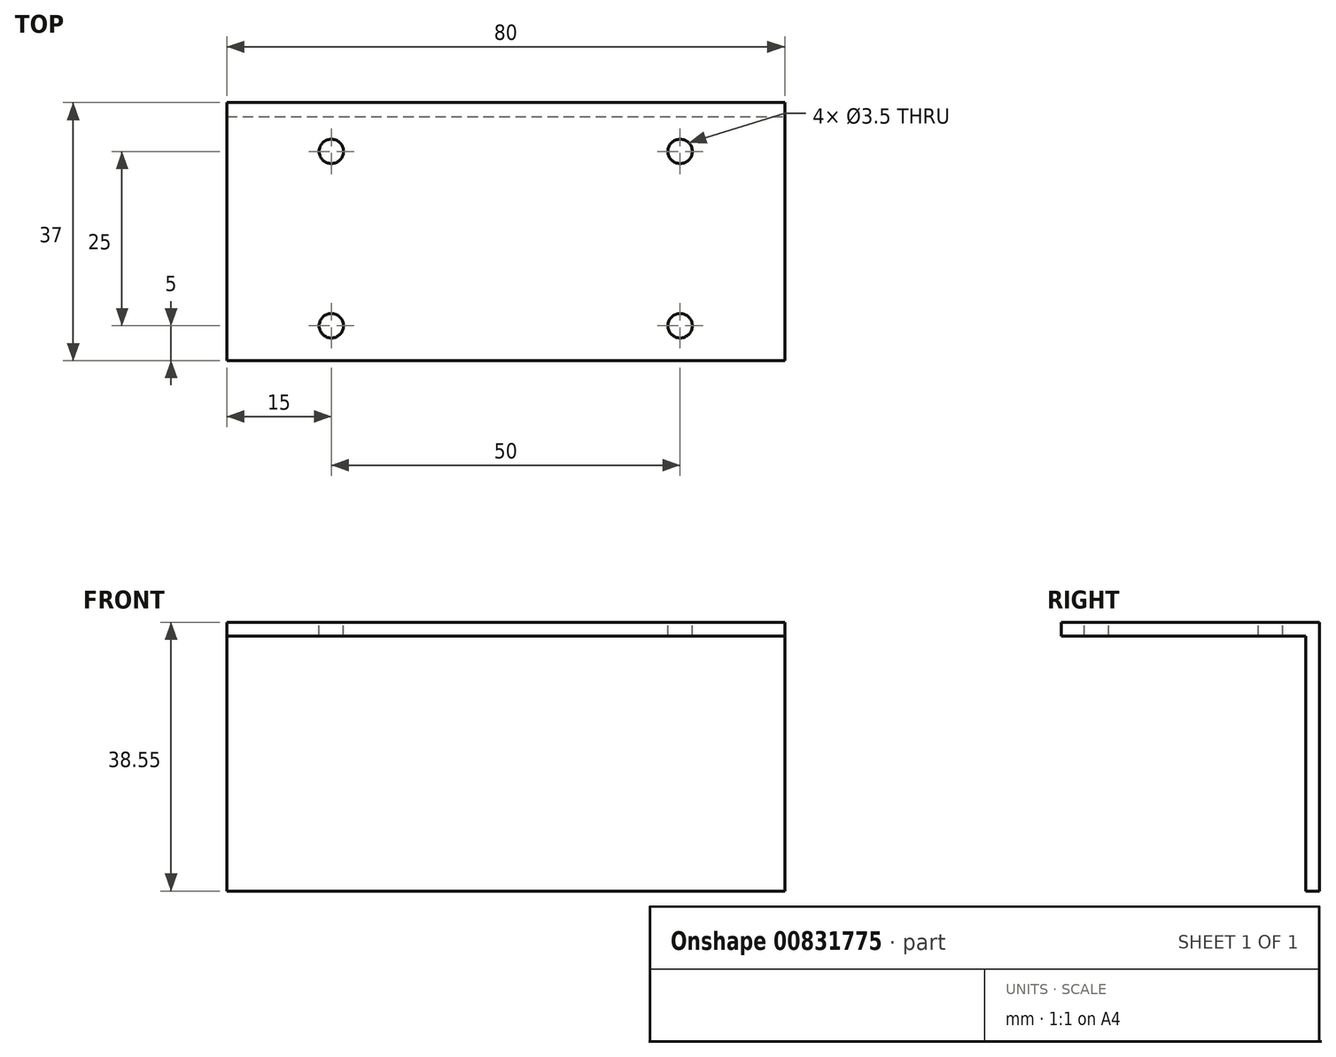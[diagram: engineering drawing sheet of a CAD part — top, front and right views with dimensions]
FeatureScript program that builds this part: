
annotation { "Feature Type Name" : "Feature", "Feature Type Description" : "" }
export const myFeature = defineFeature(function(context is Context, id is Id, definition is map)
    precondition{}
    {
        {
            var Q0;
            Q0=qCreatedBy(makeId("Top.planeOp"),FACE);
            var sketch = newSketch(context, id + "F0", { "sketchPlane" : qUnion([Q0])});
            skLineSegment(sketch, "E0.bottom", {"start": v(0, 0) * mm, "end": v(60, 0) * mm});
            skLineSegment(sketch, "E0.top", {"start": v(0, 35) * mm, "end": v(60, 35) * mm});
            skLineSegment(sketch, "E0.left", {"start": v(0, 0) * mm, "end": v(0, 35) * mm});
            skLineSegment(sketch, "E0.right", {"start": v(60, 0) * mm, "end": v(60, 35) * mm});
            skSolve(sketch);
        }
        {
            var Q0;
            Q0=makeQuery(id+"F0.imprint","IMPRINT",FACE,{"disambiguationData":[TD([[makeQuery(id+"F0.imprint","IMPRINT",EDGE,{"derivedFrom":sQuery(id+"F0.wireOp",EDGE,"E0.bottom")}),1.0]])]});
            extrude(context, id + "F1", {"entities" : qUnion([Q0]), "depth" : 2 * mm, "offsetDistance" : 25 * mm});
        }
        {
            var Q0;
            Q0=makeQuery(id+"F1.opExtrude","CAP_FACE",FACE,{"disambiguationData":[OSD([sQuery(id+"F0.wireOp",EDGE,"E0.bottom"),sQuery(id+"F0.wireOp",EDGE,"E0.top"),sQuery(id+"F0.wireOp",EDGE,"E0.left"),sQuery(id+"F0.wireOp",EDGE,"E0.right")])],"isStart":false});
            var sketch = newSketch(context, id + "F2", { "sketchPlane" : qUnion([Q0])});
            skLineSegment(sketch, "E1.bottom", {"start": v(5, 30) * mm, "end": v(55, 30) * mm, "construction": true});
            skLineSegment(sketch, "E1.top", {"start": v(5, 5) * mm, "end": v(55, 5) * mm, "construction": true});
            skLineSegment(sketch, "E1.left", {"start": v(5, 30) * mm, "end": v(5, 5) * mm, "construction": true});
            skLineSegment(sketch, "E1.right", {"start": v(55, 30) * mm, "end": v(55, 5) * mm, "construction": true});
            skCircle(sketch, "E2", {"center": v(5, 30) * mm, "radius": 1.75 * mm});
            skCircle(sketch, "E3", {"center": v(5, 5) * mm, "radius": 1.75 * mm});
            skCircle(sketch, "E4", {"center": v(55, 5) * mm, "radius": 1.75 * mm});
            skCircle(sketch, "E5", {"center": v(55, 30) * mm, "radius": 1.75 * mm});
            skSolve(sketch);
        }
        {
            var Q0;
            Q0=makeQuery(id+"F2.imprint","IMPRINT",FACE,{"disambiguationData":[TD([[makeQuery(id+"F2.imprint","IMPRINT",EDGE,{"derivedFrom":sQuery(id+"F2.wireOp",EDGE,"E3")}),1.0]])]});
            var Q1;
            Q1=makeQuery(id+"F2.imprint","IMPRINT",FACE,{"disambiguationData":[TD([[makeQuery(id+"F2.imprint","IMPRINT",EDGE,{"derivedFrom":sQuery(id+"F2.wireOp",EDGE,"E2")}),1.0]])]});
            var Q2;
            Q2=makeQuery(id+"F2.imprint","IMPRINT",FACE,{"disambiguationData":[TD([[makeQuery(id+"F2.imprint","IMPRINT",EDGE,{"derivedFrom":sQuery(id+"F2.wireOp",EDGE,"E5")}),1.0]])]});
            var Q3;
            Q3=makeQuery(id+"F2.imprint","IMPRINT",FACE,{"disambiguationData":[TD([[makeQuery(id+"F2.imprint","IMPRINT",EDGE,{"derivedFrom":sQuery(id+"F2.wireOp",EDGE,"E4")}),1.0]])]});
            extrude(context, id + "F3", {"entities" : qUnion([Q0, Q1, Q2, Q3]), "operationType" : NewBodyOperationType.REMOVE, "endBound" : BoundingType.THROUGH_ALL, "oppositeDirection" : true, "depth" : 25 * mm, "offsetDistance" : 25 * mm});
        }
        {
            var Q0;
            Q0=makeQuery(id+"F1.opExtrude","SWEPT_FACE",FACE,{"disambiguationData":[OSD([sQuery(id+"F0.wireOp",EDGE,"E0.right")])]});
            extrude(context, id + "F4", {"entities" : qUnion([Q0]), "operationType" : NewBodyOperationType.ADD, "depth" : 10 * mm, "offsetDistance" : 25 * mm});
        }
        {
            var Q0;
            Q0=makeQuery(id+"F1.opExtrude","SWEPT_FACE",FACE,{"disambiguationData":[OSD([sQuery(id+"F0.wireOp",EDGE,"E0.left")])]});
            extrude(context, id + "F5", {"entities" : qUnion([Q0]), "operationType" : NewBodyOperationType.ADD, "depth" : 10 * mm, "offsetDistance" : 25 * mm});
        }
        {
            var Q0;
            {var subQ0=sQuery(id+"F0.wireOp",EDGE,"E0.top");Q0=makeQuery(id+"F5.boolean.opBoolean","MERGE",FACE,{"derivedFrom":[makeQuery(id+"F4.boolean.opBoolean","MERGE",FACE,{"derivedFrom":[makeQuery(id+"F1.opExtrude","SWEPT_FACE",FACE,{"disambiguationData":[OSD([subQ0])]}),makeQuery(id+"F4.opExtrude","SWEPT_FACE",FACE,{"disambiguationData":[OSD([subQ0,sQuery(id+"F0.wireOp",EDGE,"E0.right")])]})]}),makeQuery(id+"F5.opExtrude","SWEPT_FACE",FACE,{"disambiguationData":[OSD([subQ0,sQuery(id+"F0.wireOp",EDGE,"E0.left")])]})]});}
            var sketch = newSketch(context, id + "F6", { "sketchPlane" : qUnion([Q0])});
            skLineSegment(sketch, "E6.bottom", {"start": v(-70, 2) * mm, "end": v(10, 2) * mm});
            skLineSegment(sketch, "E6.top", {"start": v(-70, -36.55) * mm, "end": v(10, -36.55) * mm});
            skLineSegment(sketch, "E6.left", {"start": v(-70, 2) * mm, "end": v(-70, -36.55) * mm});
            skLineSegment(sketch, "E6.right", {"start": v(10, 2) * mm, "end": v(10, -36.55) * mm});
            skSolve(sketch);
        }
        {
            var Q0;
            {var subQ0=sQuery(id+"F6.wireOp",EDGE,"E6.top");Q0=makeQuery(id+"F6.imprint","IMPRINT",FACE,{"disambiguationData":[TD([[makeQuery(id+"F6.imprint","IMPRINT",EDGE,{"derivedFrom":subQ0}),1.0]])]});}
            var Q1;
            {var subQ0=sQuery(id+"F6.wireOp",EDGE,"E6.bottom");Q1=makeQuery(id+"F6.imprint","IMPRINT",FACE,{"disambiguationData":[TD([[makeQuery(id+"F6.imprint","IMPRINT",EDGE,{"derivedFrom":subQ0}),1.0]])]});}
            extrude(context, id + "F7", {"entities" : qUnion([Q0, Q1]), "operationType" : NewBodyOperationType.ADD, "depth" : 2 * mm, "offsetDistance" : 25 * mm});
        }
    });
